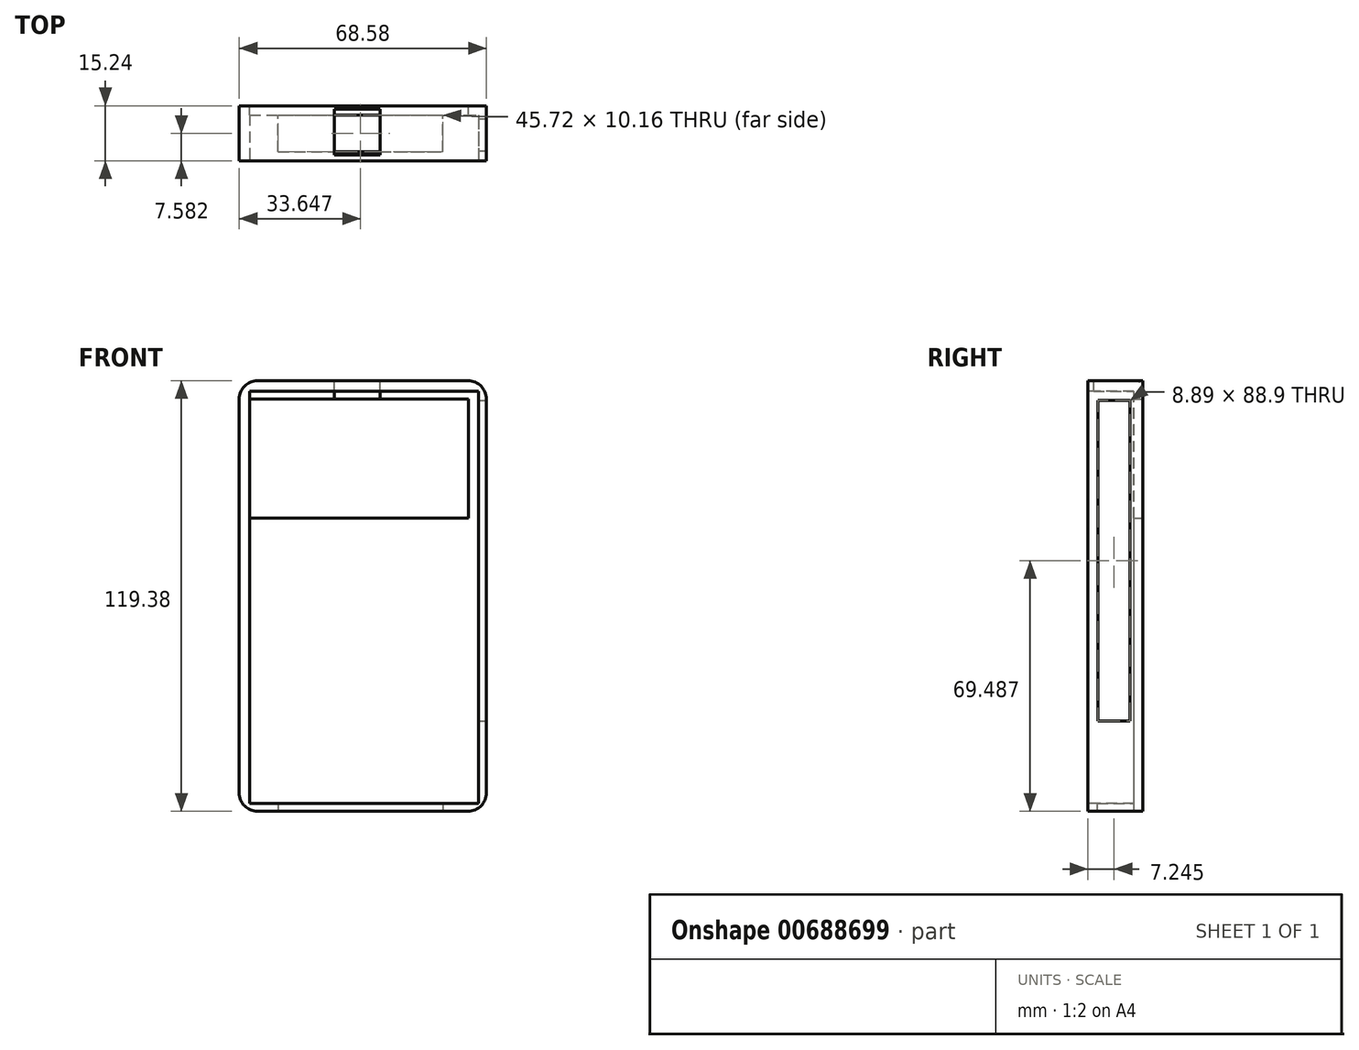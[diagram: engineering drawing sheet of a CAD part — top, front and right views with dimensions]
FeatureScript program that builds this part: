
annotation { "Feature Type Name" : "Feature", "Feature Type Description" : "" }
export const myFeature = defineFeature(function(context is Context, id is Id, definition is map)
    precondition{}
    {
        {
            var Q0;
            Q0=qCreatedBy(makeId("Front.planeOp"),FACE);
            var sketch = newSketch(context, id + "F0", { "sketchPlane" : qUnion([Q0])});
            skLineSegment(sketch, "E0.bottom", {"start": v(-76.08, -76) * mm, "end": v(-7.5, -76) * mm});
            skLineSegment(sketch, "E0.top", {"start": v(-76.08, 43.39) * mm, "end": v(-7.5, 43.39) * mm});
            skLineSegment(sketch, "E0.left", {"start": v(-76.08, -76) * mm, "end": v(-76.08, 43.39) * mm});
            skLineSegment(sketch, "E0.right", {"start": v(-7.5, -76) * mm, "end": v(-7.5, 43.39) * mm});
            skSolve(sketch);
        }
        {
            var Q0;
            Q0=makeQuery(id+"F0.imprint","IMPRINT",FACE,{"disambiguationData":[TD([[makeQuery(id+"F0.imprint","IMPRINT",EDGE,{"derivedFrom":sQuery(id+"F0.wireOp",EDGE,"E0.bottom")}),1.0]])]});
            extrude(context, id + "F1", {"entities" : qUnion([Q0]), "depth" : 15.24 * mm, "offsetDistance" : 25.4 * mm});
        }
        {
            var Q0;
            Q0=makeQuery(id+"F1.opExtrude","CAP_FACE",FACE,{"disambiguationData":[OSD([sQuery(id+"F0.wireOp",EDGE,"E0.bottom"),sQuery(id+"F0.wireOp",EDGE,"E0.top"),sQuery(id+"F0.wireOp",EDGE,"E0.left"),sQuery(id+"F0.wireOp",EDGE,"E0.right")])],"isStart":false});
            var sketch = newSketch(context, id + "F2", { "sketchPlane" : qUnion([Q0])});
            skLineSegment(sketch, "E1.bottom", {"start": v(-73.14, 40.5) * mm, "end": v(-9.64, 40.5) * mm});
            skLineSegment(sketch, "E1.top", {"start": v(-73.14, -73.8) * mm, "end": v(-9.64, -73.8) * mm});
            skLineSegment(sketch, "E1.left", {"start": v(-73.14, 40.5) * mm, "end": v(-73.14, -73.8) * mm});
            skLineSegment(sketch, "E1.right", {"start": v(-9.64, 40.5) * mm, "end": v(-9.64, -73.8) * mm});
            skSolve(sketch);
        }
        {
            var Q0;
            Q0=makeQuery(id+"F2.imprint","IMPRINT",FACE,{"disambiguationData":[TD([[makeQuery(id+"F2.imprint","IMPRINT",EDGE,{"derivedFrom":sQuery(id+"F2.wireOp",EDGE,"E1.bottom")}),-1.0]])]});
            extrude(context, id + "F3", {"entities" : qUnion([Q0]), "operationType" : NewBodyOperationType.REMOVE, "oppositeDirection" : true, "depth" : 12.7 * mm, "offsetDistance" : 25.4 * mm});
        }
        {
            var Q0;
            Q0=makeQuery(id+"F1.opExtrude","SWEPT_EDGE",EDGE,{"disambiguationData":[OSD([sQuery(id+"F0.wireOp",EDGE,"E0.top"),sQuery(id+"F0.wireOp",EDGE,"E0.right")])]});
            fillet(context, id + "F4", {"entities" : qUnion([Q0]), "radius" : 5.08 * mm, "tangentPropagation" : true, "allowEdgeOverflow" : false});
        }
        {
            var Q0;
            Q0=makeQuery(id+"F1.opExtrude","SWEPT_EDGE",EDGE,{"disambiguationData":[OSD([sQuery(id+"F0.wireOp",EDGE,"E0.top"),sQuery(id+"F0.wireOp",EDGE,"E0.left")])]});
            fillet(context, id + "F5", {"entities" : qUnion([Q0]), "radius" : 5.08 * mm, "tangentPropagation" : true, "allowEdgeOverflow" : false});
        }
        {
            var Q0;
            Q0=makeQuery(id+"F1.opExtrude","SWEPT_EDGE",EDGE,{"disambiguationData":[OSD([sQuery(id+"F0.wireOp",EDGE,"E0.bottom"),sQuery(id+"F0.wireOp",EDGE,"E0.right")])]});
            fillet(context, id + "F6", {"entities" : qUnion([Q0]), "radius" : 5.08 * mm, "tangentPropagation" : true, "allowEdgeOverflow" : false});
        }
        {
            var Q0;
            Q0=makeQuery(id+"F1.opExtrude","SWEPT_EDGE",EDGE,{"disambiguationData":[OSD([sQuery(id+"F0.wireOp",EDGE,"E0.bottom"),sQuery(id+"F0.wireOp",EDGE,"E0.left")])]});
            fillet(context, id + "F7", {"entities" : qUnion([Q0]), "radius" : 5.08 * mm, "tangentPropagation" : true, "allowEdgeOverflow" : false});
        }
        {
            var Q0;
            Q0=makeQuery(id+"F1.opExtrude","CAP_FACE",FACE,{"disambiguationData":[OSD([sQuery(id+"F0.wireOp",EDGE,"E0.bottom"),sQuery(id+"F0.wireOp",EDGE,"E0.top"),sQuery(id+"F0.wireOp",EDGE,"E0.left"),sQuery(id+"F0.wireOp",EDGE,"E0.right")])],"isStart":true});
            var sketch = newSketch(context, id + "F8", { "sketchPlane" : qUnion([Q0])});
            skSolve(sketch);
        }
        {
            var Q0;
            {var subQ2=sQuery(id+"F0.wireOp",EDGE,"E0.top");Q0=makeQuery(id+"F8.imprint","IMPRINT",FACE,{"disambiguationData":[TD([[makeQuery(id+"F8.imprint","IMPRINT",EDGE,{"derivedFrom":makeQuery(id+"F1.opExtrude","CAP_EDGE",EDGE,{"disambiguationData":[OSD([subQ2])],"isStart":true})}),1.0]])]});}
            var sketch = newSketch(context, id + "F9", { "sketchPlane" : qUnion([Q0])});
            skLineSegment(sketch, "E2.bottom", {"start": v(12.46, 38.27) * mm, "end": v(73.42, 38.27) * mm});
            skLineSegment(sketch, "E2.top", {"start": v(12.46, 5.25) * mm, "end": v(73.42, 5.25) * mm});
            skLineSegment(sketch, "E2.left", {"start": v(12.46, 38.27) * mm, "end": v(12.46, 5.25) * mm});
            skLineSegment(sketch, "E2.right", {"start": v(73.42, 38.27) * mm, "end": v(73.42, 5.25) * mm});
            skSolve(sketch);
        }
        {
            var Q0;
            Q0=makeQuery(id+"F9.imprint","IMPRINT",FACE,{"disambiguationData":[TD([[makeQuery(id+"F9.imprint","IMPRINT",EDGE,{"derivedFrom":sQuery(id+"F9.wireOp",EDGE,"E2.bottom")}),-1.0]])]});
            extrude(context, id + "F10", {"entities" : qUnion([Q0]), "operationType" : NewBodyOperationType.REMOVE, "oppositeDirection" : true, "depth" : 25.4 * mm, "offsetDistance" : 25.4 * mm});
        }
        {
            var Q0;
            Q0=makeQuery(id+"F1.opExtrude","SWEPT_FACE",FACE,{"disambiguationData":[OSD([sQuery(id+"F0.wireOp",EDGE,"E0.right")])]});
            var sketch = newSketch(context, id + "F11", { "sketchPlane" : qUnion([Q0])});
            skLineSegment(sketch, "E3.bottom", {"start": v(-12.44, 37.95) * mm, "end": v(-3.55, 37.95) * mm});
            skLineSegment(sketch, "E3.top", {"start": v(-12.44, -50.95) * mm, "end": v(-3.55, -50.95) * mm});
            skLineSegment(sketch, "E3.left", {"start": v(-12.44, 37.95) * mm, "end": v(-12.44, -50.95) * mm});
            skLineSegment(sketch, "E3.right", {"start": v(-3.55, 37.95) * mm, "end": v(-3.55, -50.95) * mm});
            skSolve(sketch);
        }
        {
            var Q0;
            Q0=makeQuery(id+"F11.imprint","IMPRINT",FACE,{"disambiguationData":[TD([[makeQuery(id+"F11.imprint","IMPRINT",EDGE,{"derivedFrom":sQuery(id+"F11.wireOp",EDGE,"E3.bottom")}),-1.0]])]});
            extrude(context, id + "F12", {"entities" : qUnion([Q0]), "operationType" : NewBodyOperationType.REMOVE, "oppositeDirection" : true, "depth" : 25.4 * mm, "offsetDistance" : 25.4 * mm});
        }
        {
            var Q0;
            Q0=makeQuery(id+"F1.opExtrude","SWEPT_FACE",FACE,{"disambiguationData":[OSD([sQuery(id+"F0.wireOp",EDGE,"E0.bottom")])]});
            var sketch = newSketch(context, id + "F13", { "sketchPlane" : qUnion([Q0])});
            skLineSegment(sketch, "E4.bottom", {"start": v(-65.3, 12.74) * mm, "end": v(-19.57, 12.74) * mm});
            skLineSegment(sketch, "E4.top", {"start": v(-65.3, 2.58) * mm, "end": v(-19.57, 2.58) * mm});
            skLineSegment(sketch, "E4.left", {"start": v(-65.3, 12.74) * mm, "end": v(-65.3, 2.58) * mm});
            skLineSegment(sketch, "E4.right", {"start": v(-19.57, 12.74) * mm, "end": v(-19.57, 2.58) * mm});
            skSolve(sketch);
        }
        {
            var Q0;
            Q0=makeQuery(id+"F13.imprint","IMPRINT",FACE,{"disambiguationData":[TD([[makeQuery(id+"F13.imprint","IMPRINT",EDGE,{"derivedFrom":sQuery(id+"F13.wireOp",EDGE,"E4.bottom")}),-1.0]])]});
            extrude(context, id + "F14", {"entities" : qUnion([Q0]), "operationType" : NewBodyOperationType.REMOVE, "oppositeDirection" : true, "depth" : 25.4 * mm, "offsetDistance" : 25.4 * mm});
        }
        {
            var Q0;
            Q0=makeQuery(id+"F1.opExtrude","SWEPT_FACE",FACE,{"disambiguationData":[OSD([sQuery(id+"F0.wireOp",EDGE,"E0.top")])]});
            var sketch = newSketch(context, id + "F15", { "sketchPlane" : qUnion([Q0])});
            skLineSegment(sketch, "E5.bottom", {"start": v(-49.63, -0.94) * mm, "end": v(-36.93, -0.94) * mm});
            skLineSegment(sketch, "E5.top", {"start": v(-49.63, -13.64) * mm, "end": v(-36.93, -13.64) * mm});
            skLineSegment(sketch, "E5.left", {"start": v(-49.63, -0.94) * mm, "end": v(-49.63, -13.64) * mm});
            skLineSegment(sketch, "E5.right", {"start": v(-36.93, -0.94) * mm, "end": v(-36.93, -13.64) * mm});
            skSolve(sketch);
        }
        {
            var Q0;
            Q0=makeQuery(id+"F15.imprint","IMPRINT",FACE,{"disambiguationData":[TD([[makeQuery(id+"F15.imprint","IMPRINT",EDGE,{"derivedFrom":sQuery(id+"F15.wireOp",EDGE,"E5.bottom")}),-1.0]])]});
            extrude(context, id + "F16", {"entities" : qUnion([Q0]), "operationType" : NewBodyOperationType.REMOVE, "oppositeDirection" : true, "depth" : 25.4 * mm, "offsetDistance" : 25.4 * mm});
        }
        {
            var Q0;
            Q0=makeQuery(id+"F10.boolean.opBoolean","COPY",FACE,{"derivedFrom":makeQuery(id+"F10.opExtrude","SWEPT_FACE",FACE,{"disambiguationData":[OSD([sQuery(id+"F9.wireOp",EDGE,"E2.top")])]})});
            var sketch = newSketch(context, id + "F17", { "sketchPlane" : qUnion([Q0])});
            skLineSegment(sketch, "E6", {"start": v(-73.42, -15.24) * mm, "end": v(-73.14, -15.24) * mm});
            skLineSegment(sketch, "E7", {"start": v(-73.14, -15.24) * mm, "end": v(-73.14, -2.54) * mm});
            skLineSegment(sketch, "E8", {"start": v(-73.14, -2.54) * mm, "end": v(-73.42, -2.54) * mm});
            skLineSegment(sketch, "E9", {"start": v(-73.42, -2.54) * mm, "end": v(-73.42, -15.24) * mm});
            skSolve(sketch);
        }
        {
            var Q0;
            {var subQ3=sQuery(id+"F17.wireOp",EDGE,"E8");Q0=makeQuery(id+"F17.imprint","IMPRINT",FACE,{"disambiguationData":[TD([[makeQuery(id+"F17.imprint","IMPRINT",EDGE,{"derivedFrom":subQ3}),-1.0]])]});}
            var sketch = newSketch(context, id + "F18", { "sketchPlane" : qUnion([Q0])});
            skLineSegment(sketch, "E10", {"start": v(-73.15, -2.54) * mm, "end": v(-73.15, 0) * mm});
            skLineSegment(sketch, "E11", {"start": v(-73.15, 0) * mm, "end": v(-73.41, 0) * mm});
            skLineSegment(sketch, "E12", {"start": v(-73.41, 0) * mm, "end": v(-73.41, -2.54) * mm});
            skLineSegment(sketch, "E13", {"start": v(-73.41, -2.54) * mm, "end": v(-73.15, -2.54) * mm});
            skSolve(sketch);
        }
        {
            var Q0;
            Q0=makeQuery(id+"F17.imprint","IMPRINT",FACE,{"disambiguationData":[TD([[makeQuery(id+"F17.imprint","IMPRINT",EDGE,{"derivedFrom":sQuery(id+"F17.wireOp",EDGE,"E6")}),1.0]])]});
            extrude(context, id + "F19", {"entities" : qUnion([Q0]), "operationType" : NewBodyOperationType.ADD, "depth" : 36.83 * mm, "offsetDistance" : 25.4 * mm});
        }
        {
            var Q0;
            {var subQ5=sQuery(id+"F18.wireOp",EDGE,"E10");Q0=makeQuery(id+"F18.imprint","IMPRINT",FACE,{"disambiguationData":[TD([[makeQuery(id+"F18.imprint","IMPRINT",EDGE,{"derivedFrom":subQ5}),1.0]])]});}
            extrude(context, id + "F20", {"entities" : qUnion([Q0]), "operationType" : NewBodyOperationType.ADD, "depth" : 36.83 * mm, "offsetDistance" : 25.4 * mm});
        }
    });
